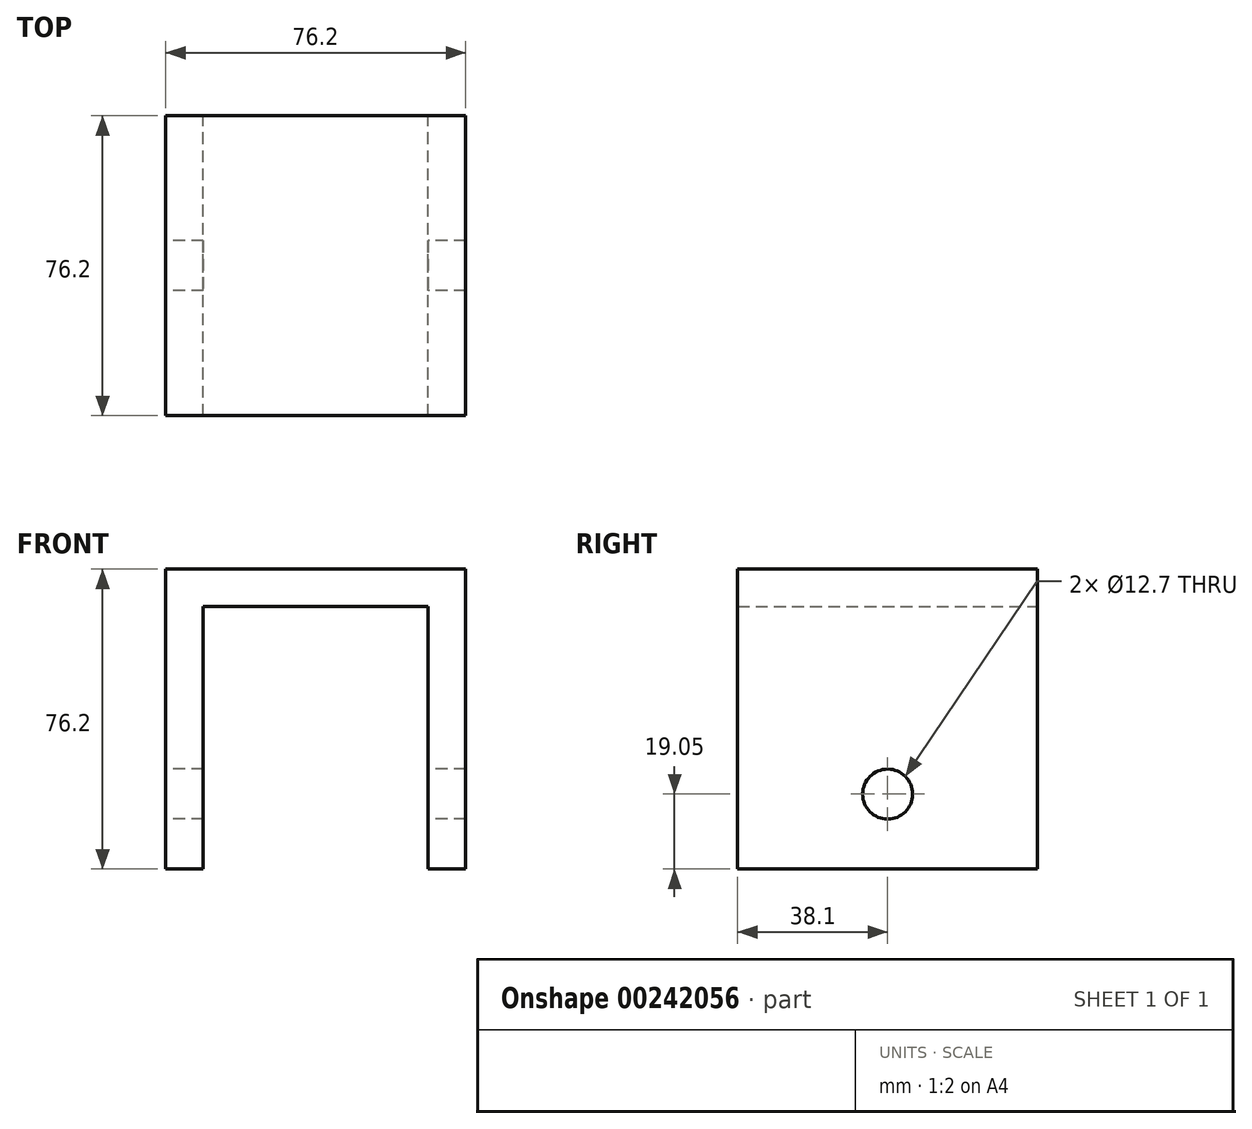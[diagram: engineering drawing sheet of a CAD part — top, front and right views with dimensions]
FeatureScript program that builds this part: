
annotation { "Feature Type Name" : "Feature", "Feature Type Description" : "" }
export const myFeature = defineFeature(function(context is Context, id is Id, definition is map)
    precondition{}
    {
        {
            var Q0;
            Q0=qCreatedBy(makeId("Front.planeOp"),FACE);
            var sketch = newSketch(context, id + "F0", { "sketchPlane" : qUnion([Q0])});
            skLineSegment(sketch, "E0.bottom", {"start": v(38.1, -38.1) * mm, "end": v(28.58, -38.1) * mm});
            skLineSegment(sketch, "E0.top", {"start": v(38.1, 38.1) * mm, "end": v(-38.1, 38.1) * mm});
            skLineSegment(sketch, "E0.left", {"start": v(38.1, -38.1) * mm, "end": v(38.1, 38.1) * mm});
            skLineSegment(sketch, "E0.right", {"start": v(-38.1, -38.1) * mm, "end": v(-38.1, 38.1) * mm});
            skPoint(sketch, "E0.middle", {"position": v(0, 0) * mm});
            skLineSegment(sketch, "E1.0", {"start": v(28.58, 28.58) * mm, "end": v(-28.57, 28.57) * mm});
            skLineSegment(sketch, "E1.1", {"start": v(28.58, -38.1) * mm, "end": v(28.58, 28.58) * mm});
            skLineSegment(sketch, "E1.3", {"start": v(-28.57, -38.1) * mm, "end": v(-28.57, 28.57) * mm});
            skLineSegment(sketch, "E2.trimOffspring", {"start": v(-28.58, -38.1) * mm, "end": v(-38.1, -38.1) * mm});
            skSolve(sketch);
        }
        {
            var Q0;
            Q0=makeQuery(id+"F0.imprint","IMPRINT",FACE,{"disambiguationData":[TD([[makeQuery(id+"F0.imprint","IMPRINT",EDGE,{"derivedFrom":sQuery(id+"F0.wireOp",EDGE,"E0.bottom")}),-1.0]])]});
            extrude(context, id + "F1", {"entities" : qUnion([Q0]), "depth" : 76.2 * mm});
        }
        {
            var Q0;
            Q0=makeQuery(id+"F1.opExtrude","SWEPT_FACE",FACE,{"disambiguationData":[OSD([sQuery(id+"F0.wireOp",EDGE,"E0.right")])]});
            var sketch = newSketch(context, id + "F2", { "sketchPlane" : qUnion([Q0])});
            skCircle(sketch, "E3", {"center": v(38.1, -19.05) * mm, "radius": 6.35 * mm});
            skSolve(sketch);
        }
        {
            var Q0;
            Q0=makeQuery(id+"F2.imprint","IMPRINT",FACE,{"disambiguationData":[TD([[makeQuery(id+"F2.imprint","IMPRINT",EDGE,{"derivedFrom":sQuery(id+"F2.wireOp",EDGE,"E3")}),1.0]])]});
            extrude(context, id + "F3", {"entities" : qUnion([Q0]), "operationType" : NewBodyOperationType.REMOVE, "endBound" : BoundingType.THROUGH_ALL, "oppositeDirection" : true, "depth" : 25.4 * mm});
        }
    });
